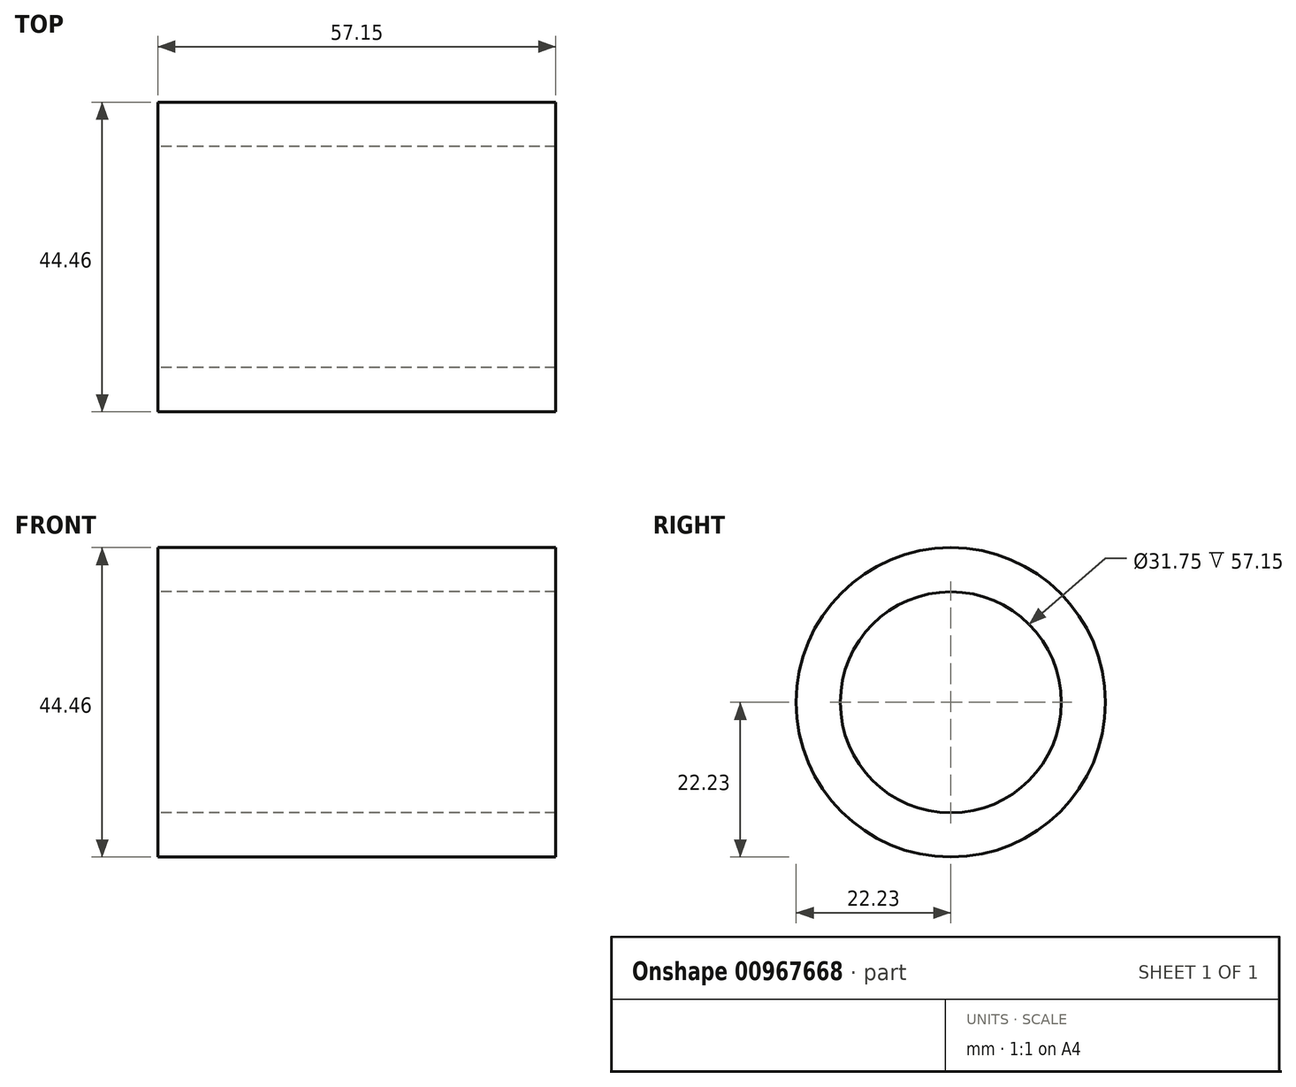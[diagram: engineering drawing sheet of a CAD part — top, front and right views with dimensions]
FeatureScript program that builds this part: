
annotation { "Feature Type Name" : "Feature", "Feature Type Description" : "" }
export const myFeature = defineFeature(function(context is Context, id is Id, definition is map)
    precondition{}
    {
        {
            var Q0;
            Q0=qCreatedBy(makeId("Right.planeOp"),FACE);
            var sketch = newSketch(context, id + "F0", { "sketchPlane" : qUnion([Q0])});
            skCircle(sketch, "E0", {"center": v(0, 0) * mm, "radius": 15.88 * mm});
            skCircle(sketch, "E1", {"center": v(0, 0) * mm, "radius": 22.23 * mm});
            skSolve(sketch);
        }
        {
            var Q0;
            Q0 = qSketchRegion(id + "F0", true);
            extrude(context, id + "F1", {"entities" : qUnion([Q0]), "depth" : 57.15 * mm, "offsetDistance" : 25.4 * mm});
        }
    });
